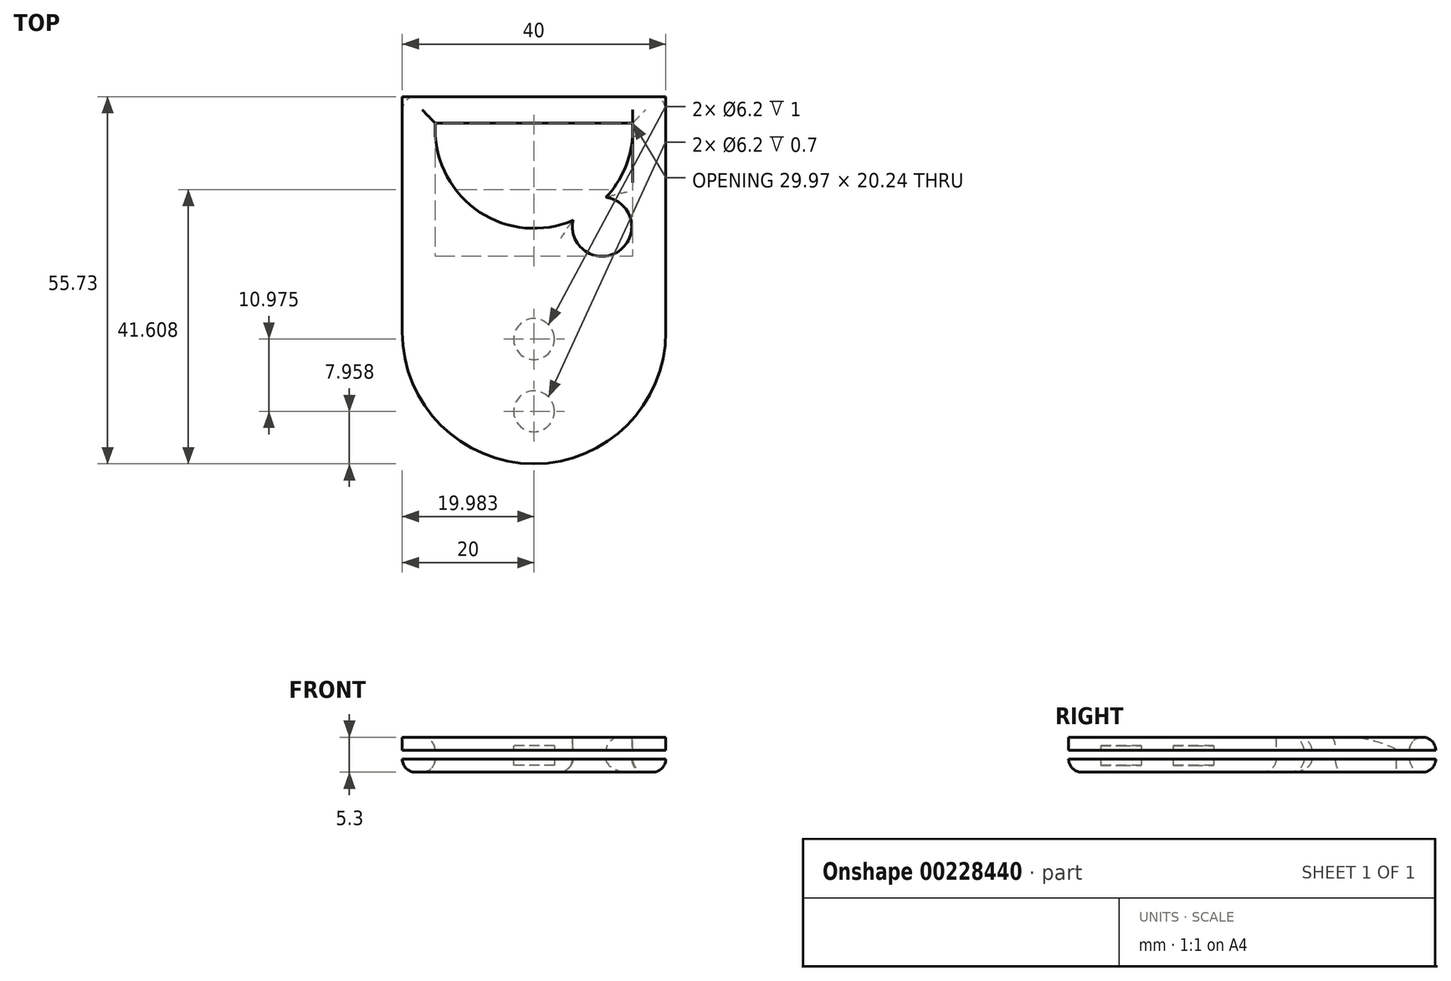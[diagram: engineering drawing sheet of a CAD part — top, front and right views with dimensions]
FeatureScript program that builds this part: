
annotation { "Feature Type Name" : "Feature", "Feature Type Description" : "" }
export const myFeature = defineFeature(function(context is Context, id is Id, definition is map)
    precondition{}
    {
        {
            var Q0;
            Q0=qCreatedBy(makeId("Top.planeOp"),FACE);
            var sketch = newSketch(context, id + "F0", { "sketchPlane" : qUnion([Q0])});
            skArc(sketch, "E0", {"start": v(-15, 0) * mm, "mid": v(-0.5, -15) * mm, "end": v(14.97, -1) * mm});
            skLineSegment(sketch, "E1.bottom", {"start": v(-20, 5) * mm, "end": v(20, 5) * mm});
            skLineSegment(sketch, "E1.left", {"start": v(-20, 5) * mm, "end": v(-20, -5) * mm});
            skLineSegment(sketch, "E1.right", {"start": v(20, 5) * mm, "end": v(20, -5) * mm});
            skPoint(sketch, "E2.start.orphan", {"position": v(20, 0) * mm});
            skPoint(sketch, "E3.start.orphan", {"position": v(-20, 0) * mm});
            skLineSegment(sketch, "E4", {"start": v(-20, -5) * mm, "end": v(-20, -50.73) * mm});
            skLineSegment(sketch, "E5", {"start": v(-20, -50.73) * mm, "end": v(20, -50.73) * mm});
            skLineSegment(sketch, "E6", {"start": v(20, -50.73) * mm, "end": v(20, -5) * mm});
            skPoint(sketch, "E7.center.orphan", {"position": v(0, -21.95) * mm});
            skArc(sketch, "E8.0", {"start": v(-18, 0) * mm, "mid": v(0, -18) * mm, "end": v(18, 0) * mm, "construction": true});
            skArc(sketch, "E9", {"start": v(-3.05, -14.69) * mm, "mid": v(0, -22.5) * mm, "end": v(3.05, -14.69) * mm});
            skLineSegment(sketch, "E10", {"start": v(0, 0) * mm, "end": v(-12.93, -18.47) * mm, "construction": true});
            skArc(sketch, "E11", {"start": v(-10.92, -10.28) * mm, "mid": v(-12.9, -18.43) * mm, "end": v(-5.93, -13.78) * mm});
            skArc(sketch, "E12.MirrorC", {"start": v(10.92, -10.28) * mm, "mid": v(12.9, -18.43) * mm, "end": v(5.93, -13.78) * mm});
            skLineSegment(sketch, "E13", {"start": v(14.97, -1) * mm, "end": v(14.97, 1) * mm});
            skLineSegment(sketch, "E14", {"start": v(14.97, 1) * mm, "end": v(-15, 1) * mm});
            skLineSegment(sketch, "E15", {"start": v(-15, 1) * mm, "end": v(-15, 0) * mm});
            skCircle(sketch, "E16", {"center": v(0, -42.77) * mm, "radius": 3.1 * mm});
            skCircle(sketch, "E17", {"center": v(0, -31.8) * mm, "radius": 3.1 * mm});
            skSolve(sketch);
        }
        {
            var Q0;
            Q0=makeQuery(id+"F0.imprint","IMPRINT",FACE,{"disambiguationData":[TD([[makeQuery(id+"F0.imprint","IMPRINT",EDGE,{"derivedFrom":sQuery(id+"F0.wireOp",EDGE,"E0")}),-1.0]])]});
            var Q1;
            {var subQ0=sQuery(id+"F0.wireOp",EDGE,"E7");var subQ1=sQuery(id+"F0.wireOp",EDGE,"E0");var subQ2=makeQuery(id+"F0.imprint","INTERSECT",VERTEX,{"disambiguationData":[OD(0.0)],"derivedFrom":[subQ1,subQ0]});Q1=makeQuery(id+"F0.imprint","IMPRINT",FACE,{"disambiguationData":[TD([[makeQuery(id+"F0.imprint","IMPRINT",EDGE,{"disambiguationData":[TD([[subQ2,-1.0]])],"derivedFrom":subQ1}),-1.0]])]});}
            var Q2;
            {var subQ0=sQuery(id+"F0.wireOp",EDGE,"E11");Q2=makeQuery(id+"F0.imprint","IMPRINT",FACE,{"disambiguationData":[TD([[makeQuery(id+"F0.imprint","IMPRINT",EDGE,{"derivedFrom":subQ0}),1.0]])]});}
            var Q3;
            {var subQ0=sQuery(id+"F0.wireOp",EDGE,"E9");Q3=makeQuery(id+"F0.imprint","IMPRINT",FACE,{"disambiguationData":[TD([[makeQuery(id+"F0.imprint","IMPRINT",EDGE,{"derivedFrom":subQ0}),1.0]])]});}
            var Q4;
            {var subQ0=sQuery(id+"F0.wireOp",EDGE,"E12.MirrorC");Q4=makeQuery(id+"F0.imprint","IMPRINT",FACE,{"disambiguationData":[TD([[makeQuery(id+"F0.imprint","IMPRINT",EDGE,{"derivedFrom":subQ0}),-1.0]])]});}
            var Q5;
            Q5=makeQuery(id+"F0.imprint","IMPRINT",FACE,{"disambiguationData":[TD([[makeQuery(id+"F0.imprint","IMPRINT",EDGE,{"derivedFrom":sQuery(id+"F0.wireOp",EDGE,"E16")}),1.0]])]});
            var Q6;
            Q6=makeQuery(id+"F0.imprint","IMPRINT",FACE,{"disambiguationData":[TD([[makeQuery(id+"F0.imprint","IMPRINT",EDGE,{"derivedFrom":sQuery(id+"F0.wireOp",EDGE,"E17")}),1.0]])]});
            extrude(context, id + "F1", {"entities" : qUnion([Q0, Q1, Q2, Q3, Q4, Q5, Q6]), "depth" : 5.3 * mm, "offsetDistance" : 25 * mm});
        }
        {
            var Q0;
            {var subQ0=sQuery(id+"F0.wireOp",EDGE,"E11");Q0=makeQuery(id+"F0.imprint","IMPRINT",FACE,{"disambiguationData":[TD([[makeQuery(id+"F0.imprint","IMPRINT",EDGE,{"derivedFrom":subQ0}),1.0]])]});}
            var Q1;
            {var subQ0=sQuery(id+"F0.wireOp",EDGE,"E9");Q1=makeQuery(id+"F0.imprint","IMPRINT",FACE,{"disambiguationData":[TD([[makeQuery(id+"F0.imprint","IMPRINT",EDGE,{"derivedFrom":subQ0}),1.0]])]});}
            var Q2;
            {var subQ0=sQuery(id+"F0.wireOp",EDGE,"E12.MirrorC");Q2=makeQuery(id+"F0.imprint","IMPRINT",FACE,{"disambiguationData":[TD([[makeQuery(id+"F0.imprint","IMPRINT",EDGE,{"derivedFrom":subQ0}),-1.0]])]});}
            extrude(context, id + "F2", {"entities" : qUnion([Q0, Q1, Q2]), "operationType" : NewBodyOperationType.REMOVE, "depth" : 3.3 * mm, "hasSecondDirection" : true, "secondDirectionOppositeDirection" : false, "secondDirectionDepth" : 2 * mm, "offsetDistance" : 25 * mm});
        }
        {
            var Q0;
            Q0=makeQuery(id+"F0.imprint","IMPRINT",FACE,{"disambiguationData":[TD([[makeQuery(id+"F0.imprint","IMPRINT",EDGE,{"derivedFrom":sQuery(id+"F0.wireOp",EDGE,"E16")}),1.0]])]});
            var Q1;
            Q1=makeQuery(id+"F0.imprint","IMPRINT",FACE,{"disambiguationData":[TD([[makeQuery(id+"F0.imprint","IMPRINT",EDGE,{"derivedFrom":sQuery(id+"F0.wireOp",EDGE,"E17")}),1.0]])]});
            extrude(context, id + "F3", {"entities" : qUnion([Q0, Q1]), "operationType" : NewBodyOperationType.REMOVE, "depth" : 4 * mm, "hasSecondDirection" : true, "secondDirectionOppositeDirection" : false, "secondDirectionDepth" : 1 * mm});
        }
        {
            var Q0;
            Q0=makeQuery(id+"F1.opExtrude","CAP_EDGE",EDGE,{"disambiguationData":[OSD([sQuery(id+"F0.wireOp",EDGE,"E14")])],"isStart":false});
            var Q1;
            Q1=makeQuery(id+"F1.opExtrude","CAP_EDGE",EDGE,{"disambiguationData":[OSD([sQuery(id+"F0.wireOp",EDGE,"E14")])],"isStart":true});
            var Q2;
            Q2=makeQuery(id+"F1.opExtrude","CAP_EDGE",EDGE,{"disambiguationData":[OSD([sQuery(id+"F0.wireOp",EDGE,"E1.bottom")])],"isStart":false});
            var Q3;
            Q3=makeQuery(id+"F1.opExtrude","CAP_EDGE",EDGE,{"disambiguationData":[OSD([sQuery(id+"F0.wireOp",EDGE,"E1.bottom")])],"isStart":true});
            fillet(context, id + "F4", {"entities" : qUnion([Q0, Q1, Q2, Q3]), "radius" : 2 * mm, "tangentPropagation" : true, "allowEdgeOverflow" : false});
        }
        {
            var Q0;
            Q0=makeQuery(id+"F1.opExtrude","SWEPT_EDGE",EDGE,{"disambiguationData":[OSD([sQuery(id+"F0.wireOp",EDGE,"E5"),sQuery(id+"F0.wireOp",EDGE,"E6")])]});
            var Q1;
            Q1=makeQuery(id+"F1.opExtrude","SWEPT_EDGE",EDGE,{"disambiguationData":[OSD([sQuery(id+"F0.wireOp",EDGE,"E4"),sQuery(id+"F0.wireOp",EDGE,"E5")])]});
            fillet(context, id + "F5", {"entities" : qUnion([Q0, Q1]), "radius" : 20 * mm, "tangentPropagation" : true, "allowEdgeOverflow" : false});
        }
        {
            var Q0;
            Q0=makeQuery(id+"F1.opExtrude","CAP_EDGE",EDGE,{"disambiguationData":[OSD([sQuery(id+"F0.wireOp",EDGE,"E0")])],"isStart":true});
            var Q1;
            Q1=makeQuery(id+"F1.opExtrude","CAP_FACE",FACE,{"disambiguationData":[OSD([sQuery(id+"F0.wireOp",EDGE,"E0"),sQuery(id+"F0.wireOp",EDGE,"E1.bottom"),sQuery(id+"F0.wireOp",EDGE,"E1.left"),sQuery(id+"F0.wireOp",EDGE,"E1.right"),sQuery(id+"F0.wireOp",EDGE,"VS0sWyAE-EdNi-RvXL-zYZn-pJlJ5YTStzKs"),sQuery(id+"F0.wireOp",EDGE,"E4"),sQuery(id+"F0.wireOp",EDGE,"E5"),sQuery(id+"F0.wireOp",EDGE,"E6")])],"isStart":true});
            var Q2;
            Q2=makeQuery(id+"F1.opExtrude","CAP_EDGE",EDGE,{"disambiguationData":[OSD([sQuery(id+"F0.wireOp",EDGE,"E0")])],"isStart":false});
            fillet(context, id + "F6", {"entities" : qUnion([Q0, Q1, Q2]), "radius" : 2 * mm, "tangentPropagation" : true, "allowEdgeOverflow" : false});
        }
    });
